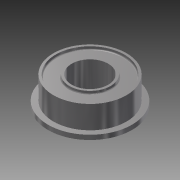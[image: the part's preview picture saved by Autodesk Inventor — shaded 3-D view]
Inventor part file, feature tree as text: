
AUTODESK INVENTOR PART (.ipt)
format: ipt  version: 2013 (Build 170138000, 138)  size: 155,136 bytes
history: native  units: mm
features: sketch x5, extrude x4, other x1, hole x1, fillet x1
ambient origin geometry x1: Origin
feature tree (12):
  other  "ソリッド1"
  extrude  "押し出し1"  Depth=9.2mm
  extrude  "押し出し2"  Depth=0.5mm TaperAngle=0.0deg
  hole  "穴1"  [1 undecoded]
  extrude  "押し出し3"  Depth=2.5mm TaperAngle=0.0deg
  extrude  "押し出し4"  Depth=4.0mm
  fillet  "フィレット1"  Radius=4.5mm
  sketch  "スケッチ1"
  sketch  "スケッチ2"
  sketch  "スケッチ3"
  sketch  "スケッチ4"
  sketch  "スケッチ5"
note: 1 required parameter value undecoded (feature->parameter linkage not recoverable at this tier; creation-order binding heuristic only, values carry confidence <= 0.55)
